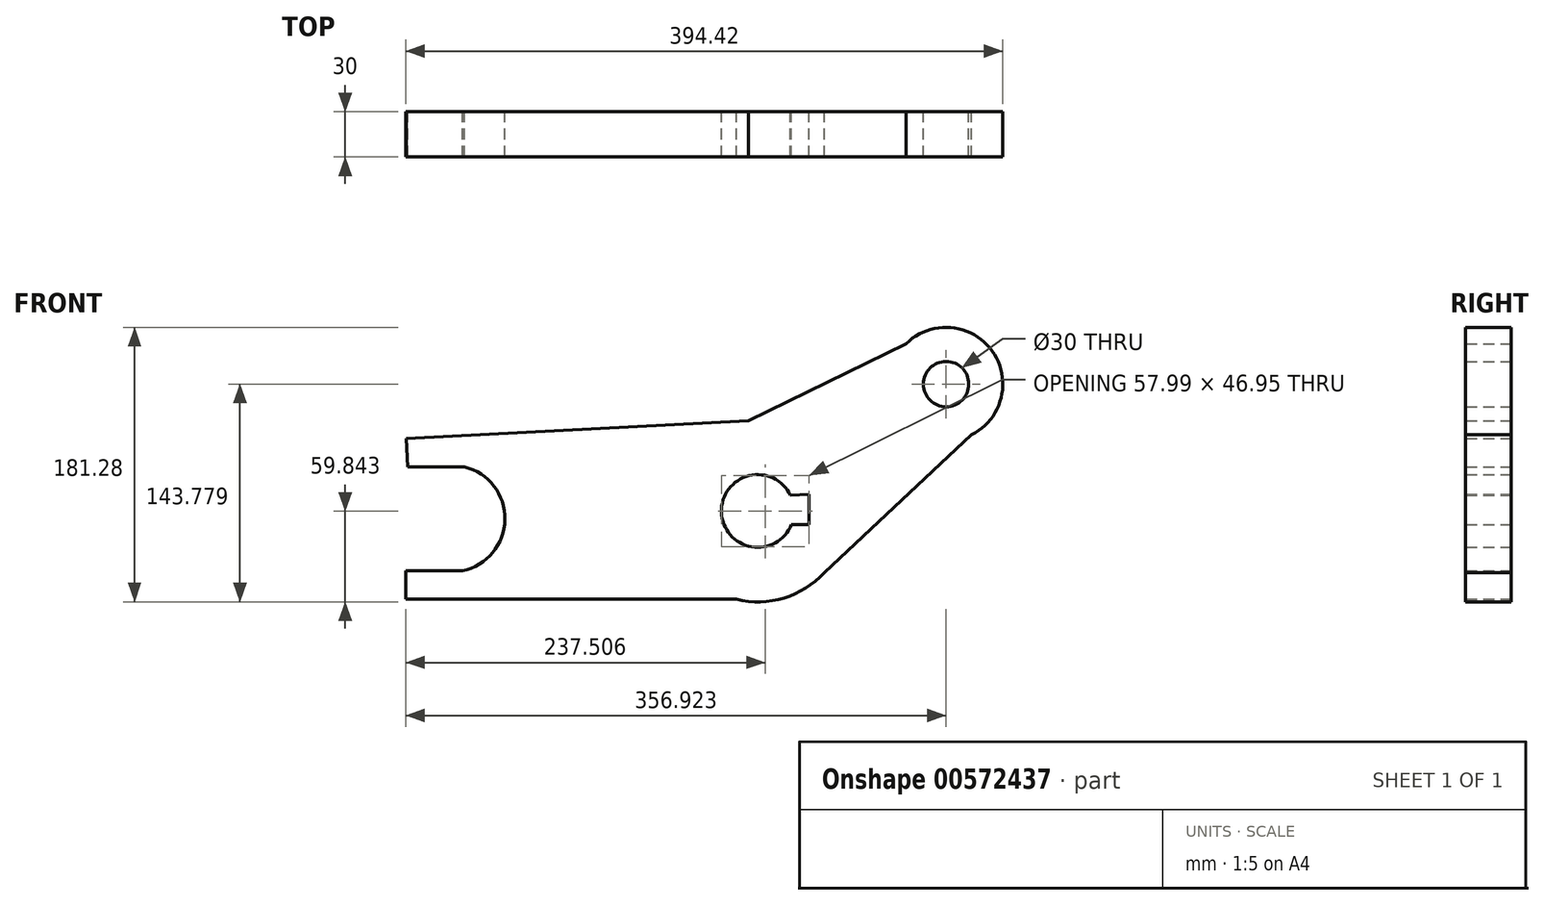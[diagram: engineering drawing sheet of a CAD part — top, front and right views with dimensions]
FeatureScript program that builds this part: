
annotation { "Feature Type Name" : "Feature", "Feature Type Description" : "" }
export const myFeature = defineFeature(function(context is Context, id is Id, definition is map)
    precondition{}
    {
        {
            var Q0;
            Q0=qCreatedBy(makeId("Front.planeOp"),FACE);
            var sketch = newSketch(context, id + "F0", { "sketchPlane" : qUnion([Q0])});
            skCircle(sketch, "E0", {"center": v(0, 0) * mm, "radius": 60 * mm});
            skCircle(sketch, "E1", {"center": v(124.42, 83.78) * mm, "radius": 15 * mm});
            skCircle(sketch, "E2", {"center": v(124.42, 83.78) * mm, "radius": 37.5 * mm});
            skArc(sketch, "E3", {"start": v(21.64, 10.37) * mm, "mid": v(-23.99, -0.76) * mm, "end": v(22.25, -8.99) * mm});
            skLineSegment(sketch, "E4", {"start": v(-14.04, -58.33) * mm, "end": v(-232.5, -58.33) * mm});
            skLineSegment(sketch, "E5", {"start": v(-232.5, -58.33) * mm, "end": v(-232.5, -39.52) * mm});
            skLineSegment(sketch, "E6", {"start": v(-232.5, -39.52) * mm, "end": v(-195, -39.52) * mm});
            skPoint(sketch, "E7.start.orphan", {"position": v(-230.2, 0) * mm});
            skPoint(sketch, "E8.orphan", {"position": v(-195, 0) * mm});
            skLineSegment(sketch, "E9", {"start": v(0, 60) * mm, "end": v(-232.19, 47.97) * mm});
            skLineSegment(sketch, "E10", {"start": v(-232.19, 47.97) * mm, "end": v(-231.22, 29.19) * mm});
            skLineSegment(sketch, "E11", {"start": v(-231.22, 29.19) * mm, "end": v(-193.72, 29.19) * mm});
            skArc(sketch, "E12", {"start": v(-195, -39.52) * mm, "mid": v(-167, -5.68) * mm, "end": v(-193.72, 29.19) * mm});
            skLineSegment(sketch, "E13", {"start": v(-167, -4.36) * mm, "end": v(-59.84, -4.36) * mm});
            skPoint(sketch, "E13.startSnap0", {"position": v(-167, -5.68) * mm});
            skLineSegment(sketch, "E14", {"start": v(-6.2, 59.68) * mm, "end": v(98.12, 110.5) * mm});
            skLineSegment(sketch, "E15", {"start": v(37.86, -46.55) * mm, "end": v(141.28, 50.28) * mm});
            skLineSegment(sketch, "E16", {"start": v(34, 11.01) * mm, "end": v(34, -8.99) * mm});
            skLineSegment(sketch, "E17", {"start": v(34, -8.99) * mm, "end": v(22.25, -8.99) * mm});
            skLineSegment(sketch, "E18", {"start": v(34, 11.01) * mm, "end": v(21.64, 10.37) * mm});
            skLineSegment(sketch, "E19", {"start": v(112.42, 74.78) * mm, "end": v(57.32, 17.72) * mm});
            skSolve(sketch);
        }
        {
            var Q0;
            Q0 = qSketchRegion(id + "F0", true);
            extrude(context, id + "F1", {"entities" : qUnion([Q0]), "depth" : 30 * mm, "offsetDistance" : 25 * mm});
        }
    });
